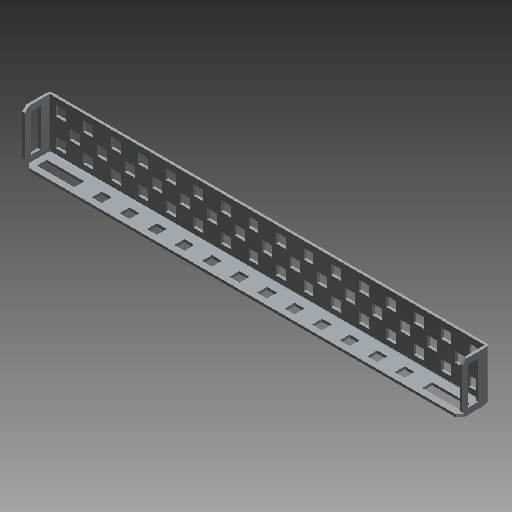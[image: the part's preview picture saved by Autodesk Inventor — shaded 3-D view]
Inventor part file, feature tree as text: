
AUTODESK INVENTOR PART (.ipt)
format: ipt  version: 2018 (Build 220112000, 112)  size: 761,344 bytes
history: native  units: mm (DEFAULTED — no unit token found)
features: other x75, extrude x67, sketch x12, sheet_metal_op x7, pattern_linear x3
ambient origin geometry x8: Origin, YZ Plane, XZ Plane, XY Plane, X Axis, Y Axis, Z Axis, Center Point
bodies: Solid1 (feature_tree)
feature tree (164):
  sheet_metal_op  "Face1"
  sheet_metal_op  "Flange5"
  sheet_metal_op  "Flange6"
  other  "Corner Chamfer2"
  sheet_metal_op  "Flange7"
  other  "Corner Chamfer3"
  pattern_linear  "Rectangular Pattern1"  Count1=15 Spacing1=12.7mm
  pattern_linear  "Rectangular Pattern2"  Spacing1=11.5316mm  [1 undecoded]
  pattern_linear  "Rectangular Pattern3"  Spacing1=1.17mm  [1 undecoded]
  sketch  "Sketch17"  dims[d65=0.585mm]
  sketch  "Sketch18"  dims[d66=2.34mm]
  sketch  "Sketch19"  dims[d67=0.381mm d68=11.5316mm d69=90.0deg d70=0.381mm d71=1.17mm d72=0.585mm d73=2.34mm d74=0.381mm d75=11.5316mm d76=90.0deg d77=0.381mm d84=1.905mm d85=6.35mm d86=45.0deg d88=17.272mm d89=2.794mm d90=2.794mm d91=4.572mm d92=4.572mm d93=8.128mm d94=120.0mm d96=12.7mm d97=10.0mm d99=25.4mm d102=8.128mm d103=2.794mm d104=1.17mm d105=0.585mm d106=2.34mm d107=0.381mm d108=11.5316mm d109=90.0deg d110=0.381mm d111=4.572mm d112=2.794mm d113=1.17mm d114=0.0mm d115=1.905mm d116=6.35mm d117=45.0deg d118=2.794mm d119=2.794mm d121=17.272mm d122=4.572mm d123=1.17mm d124=0.0mm d125=25.4mm d126=0.0mm d127=160.0mm d129=12.7mm d130=20.0mm d132=12.7mm d133=25.4mm d134=0.0mm d135=150.0mm d137=12.7mm d138=25.4mm d139=0.0mm d140=120.0mm d142=12.7mm d143=0.0mm d144=0.0mm d145=0.0mm d146=0.0mm d147=0.0mm d148=0.0mm d149=0.0mm d150=0.0mm d151=0.0mm d152=0.0mm d153=0.0mm d154=0.0mm d155=0.0mm d156=0.0mm d157=0.0mm d158=0.0mm d159=0.0mm d160=0.0mm d161=0.0mm d162=0.0mm d163=0.0mm d164=0.0mm d165=0.0mm d166=0.0mm d167=0.0mm d168=0.0mm d169=0.0mm d170=0.0mm d171=0.0mm d172=0.0mm d173=0.0mm d174=0.0mm d175=0.0mm d176=0.0mm d177=0.0mm d178=0.0mm d179=0.0mm d180=0.0mm d181=0.0mm d182=0.0mm d183=0.0mm d184=0.0mm d185=0.0mm d186=0.0mm d187=0.0mm d188=0.0mm d189=0.0mm d190=6.35mm d191=9.144mm d192=0.0mm d193=0.0mm d194=0.0mm d195=0.0mm d196=0.0mm d197=0.0mm d198=0.0mm d199=0.0mm d200=0.0mm d201=0.0mm d202=0.0mm d203=0.0mm d204=0.0mm d205=0.0mm d206=0.0mm d207=0.0mm d208=0.0mm d209=0.0mm d210=0.0mm d211=0.0mm d212=0.0mm d213=0.0mm d214=0.0mm d215=0.0mm d216=0.0mm d217=0.0mm d218=0.0mm d219=0.0mm d220=0.0mm d221=0.0mm d222=0.0mm d223=0.0mm d224=0.0mm d225=0.0mm d226=0.0mm d227=0.0mm d228=0.0mm d229=0.0mm d230=0.0mm d231=0.0mm d232=0.0mm d233=0.0mm d234=0.0mm d235=0.0mm d236=0.0mm d237=0.0mm d238=0.0mm d239=0.0mm d240=0.0mm d241=0.0mm d242=0.0mm d243=0.0mm d244=0.0mm d245=0.0mm d246=0.0mm d247=0.0mm d248=0.0mm d249=0.0mm d250=0.0mm d251=0.0mm d252=0.0mm d253=0.0mm d254=0.0mm d255=0.0mm d256=0.0mm d257=0.0mm d258=0.0mm d259=0.0mm d260=0.0mm d261=0.0mm d262=0.0mm d263=25.4mm d264=0.0mm d265=25.4mm d266=0.0mm d267=25.4mm d268=0.0mm d269=25.4mm d270=0.0mm d271=0.0mm d272=0.0mm d273=0.0mm d274=0.0mm d275=0.0mm d276=0.0mm d277=0.0mm d278=0.0mm d279=25.4mm d280=0.0mm d281=25.4mm d282=0.0mm d283=25.4mm d284=0.0mm d285=25.4mm d286=0.0mm d287=0.0mm d288=0.0mm d289=0.0mm d290=0.0mm d291=0.0mm d292=0.0mm d293=0.0mm d294=0.0mm d295=1.17mm]
  sketch  "Sketch1"  dims[d20=2.794mm]
  other  "Plate1"
  sketch  "Sketch7"  dims[d21=2.794mm]
  other  "Plate6"
  sheet_metal_op  "Bend5"
  sketch  "Sketch8"  dims[d22=2.921mm]
  other  "Plate7"
  sheet_metal_op  "Bend6"
  sketch  "Sketch11"  dims[d23=22.86mm]
  sketch  "Sketch12"  dims[d24=4.6228mm]
  other  "Plate8"
  sheet_metal_op  "Bend7"
  sketch  "Sketch13"  dims[d25=8.128mm]
  sketch  "Sketch14"  dims[d26=4.6228mm]
  other  "Srf1"
  other  "Srf2"
  other  "Srf3"
  other  "Srf4"
  other  "Srf5"
  other  "Srf6"
  other  "Srf7"
  other  "Srf8"
  other  "Srf9"
  other  "Srf10"
  other  "Srf11"
  other  "Srf12"
  other  "Srf13"
  other  "Srf14"
  other  "Srf15"
  other  "Srf16"
  other  "Srf17"
  other  "Srf18"
  other  "Srf19"
  other  "Srf20"
  other  "Srf21"
  other  "Srf22"
  other  "Srf23"
  other  "Srf24"
  other  "Srf25"
  other  "Srf26"
  other  "Srf27"
  other  "Srf28"
  other  "Srf29"
  other  "Srf30"
  other  "Srf31"
  other  "Srf32"
  sketch  "Sketch15"  dims[d27=0.381mm]
  other  "Srf33"
  other  "Srf34"
  other  "Srf35"
  other  "Srf36"
  other  "Srf37"
  other  "Srf38"
  other  "Srf39"
  other  "Srf40"
  other  "Srf41"
  other  "Srf42"
  other  "Srf43"
  other  "Srf44"
  other  "Srf45"
  other  "Srf46"
  other  "Srf47"
  sketch  "Sketch16"  dims[d64=1.17mm]
  other  "Srf48"
  other  "Srf49"
  other  "Srf50"
  other  "Srf51"
  other  "Srf52"
  other  "Srf53"
  other  "Srf54"
  other  "Srf55"
  other  "Srf56"
  other  "Srf57"
  other  "Srf58"
  other  "Srf59"
  other  "Srf60"
  other  "Srf61"
  other  "Srf62"
  other  "Srf63"
  other  "Srf64"
  other  "Srf65"
  other  "Srf66"
  other  "Srf67"
  other  "Cut2"
  other  "Cut3"
  extrude  "ExtrusionSrf1"  Depth=1.17mm
  extrude  "ExtrusionSrf33"  Depth=1.17mm
  extrude  "ExtrusionSrf48"  Depth=0.381mm
  extrude  "ExtrusionSrf60"  Depth=11.5316mm TaperAngle=90.0deg
  extrude  "ExtrusionSrf61"  Depth=6.35mm TaperAngle=45.0deg
  extrude  "ExtrusionSrf62"  Depth=17.272mm
  extrude  "ExtrusionSrf63"  Depth=2.794mm
  extrude  "ExtrusionSrf64"  Depth=2.794mm
  extrude  "ExtrusionSrf65"  Depth=4.572mm
  extrude  "ExtrusionSrf66"  Depth=4.572mm
  extrude  "ExtrusionSrf67"  Depth=8.128mm
  extrude  "ExtrusionSrf2"  Depth=12.7mm
  extrude  "ExtrusionSrf3"  Depth=8.128mm
  extrude  "ExtrusionSrf4"  Depth=2.794mm
  extrude  "ExtrusionSrf5"  Depth=1.17mm
  extrude  "ExtrusionSrf6"  Depth=1.17mm
  extrude  "ExtrusionSrf7"  Depth=1.17mm
  extrude  "ExtrusionSrf8"  Depth=0.381mm
  extrude  "ExtrusionSrf9"  Depth=11.5316mm TaperAngle=90.0deg
  extrude  "ExtrusionSrf10"  Depth=4.572mm
  extrude  "ExtrusionSrf11"  Depth=2.794mm
  extrude  "ExtrusionSrf12"  Depth=1.17mm
  extrude  "ExtrusionSrf13"  TaperAngle=0.0deg  [1 undecoded]
  extrude  "ExtrusionSrf14"  Depth=6.35mm TaperAngle=45.0deg
  extrude  "ExtrusionSrf15"  Depth=2.794mm
  extrude  "ExtrusionSrf16"  Depth=2.794mm
  extrude  "ExtrusionSrf17"  Depth=17.272mm
  extrude  "ExtrusionSrf18"  Depth=4.572mm
  extrude  "ExtrusionSrf19"  Depth=1.17mm
  extrude  "ExtrusionSrf20"  TaperAngle=0.0deg  [1 undecoded]
  extrude  "ExtrusionSrf21"  Depth=25.4mm TaperAngle=0.0deg
  extrude  "ExtrusionSrf22"  Depth=12.7mm
  extrude  "ExtrusionSrf23"  Depth=12.7mm
  extrude  "ExtrusionSrf24"  Depth=25.4mm TaperAngle=0.0deg
  extrude  "ExtrusionSrf25"  Depth=150.0mm
  extrude  "ExtrusionSrf26"  Depth=25.4mm TaperAngle=0.0deg
  extrude  "ExtrusionSrf27"  Depth=12.7mm
  extrude  "ExtrusionSrf28"  TaperAngle=0.0deg  [1 undecoded]
  extrude  "ExtrusionSrf29"  TaperAngle=0.0deg  [1 undecoded]
  extrude  "ExtrusionSrf30"  TaperAngle=0.0deg  [1 undecoded]
  extrude  "ExtrusionSrf31"  TaperAngle=0.0deg  [1 undecoded]
  extrude  "ExtrusionSrf32"  TaperAngle=0.0deg  [1 undecoded]
  extrude  "ExtrusionSrf34"  TaperAngle=0.0deg  [1 undecoded]
  extrude  "ExtrusionSrf35"  TaperAngle=0.0deg  [1 undecoded]
  extrude  "ExtrusionSrf36"  TaperAngle=0.0deg  [1 undecoded]
  extrude  "ExtrusionSrf37"  TaperAngle=0.0deg  [1 undecoded]
  extrude  "ExtrusionSrf38"  TaperAngle=0.0deg  [1 undecoded]
  extrude  "ExtrusionSrf39"  TaperAngle=0.0deg  [1 undecoded]
  extrude  "ExtrusionSrf40"  TaperAngle=0.0deg  [1 undecoded]
  extrude  "ExtrusionSrf41"  TaperAngle=0.0deg  [1 undecoded]
  extrude  "ExtrusionSrf42"  TaperAngle=0.0deg  [1 undecoded]
  extrude  "ExtrusionSrf43"  TaperAngle=0.0deg  [1 undecoded]
  extrude  "ExtrusionSrf44"  TaperAngle=0.0deg  [1 undecoded]
  extrude  "ExtrusionSrf45"  TaperAngle=0.0deg  [1 undecoded]
  extrude  "ExtrusionSrf46"  TaperAngle=0.0deg  [1 undecoded]
  extrude  "ExtrusionSrf47"  TaperAngle=0.0deg  [1 undecoded]
  extrude  "ExtrusionSrf49"  TaperAngle=0.0deg  [1 undecoded]
  extrude  "ExtrusionSrf50"  TaperAngle=0.0deg  [1 undecoded]
  extrude  "ExtrusionSrf51"  TaperAngle=0.0deg  [1 undecoded]
  extrude  "ExtrusionSrf52"  TaperAngle=0.0deg  [1 undecoded]
  extrude  "ExtrusionSrf53"  TaperAngle=0.0deg  [1 undecoded]
  extrude  "ExtrusionSrf54"  TaperAngle=0.0deg  [1 undecoded]
  extrude  "ExtrusionSrf55"  TaperAngle=0.0deg  [1 undecoded]
  extrude  "ExtrusionSrf56"  TaperAngle=0.0deg  [1 undecoded]
  extrude  "ExtrusionSrf57"  TaperAngle=0.0deg  [1 undecoded]
  extrude  "ExtrusionSrf58"  TaperAngle=0.0deg  [1 undecoded]
  extrude  "ExtrusionSrf59"  TaperAngle=0.0deg  [1 undecoded]
note: 34 required parameter values undecoded (feature->parameter linkage not recoverable at this tier; creation-order binding heuristic only, values carry confidence <= 0.55)
